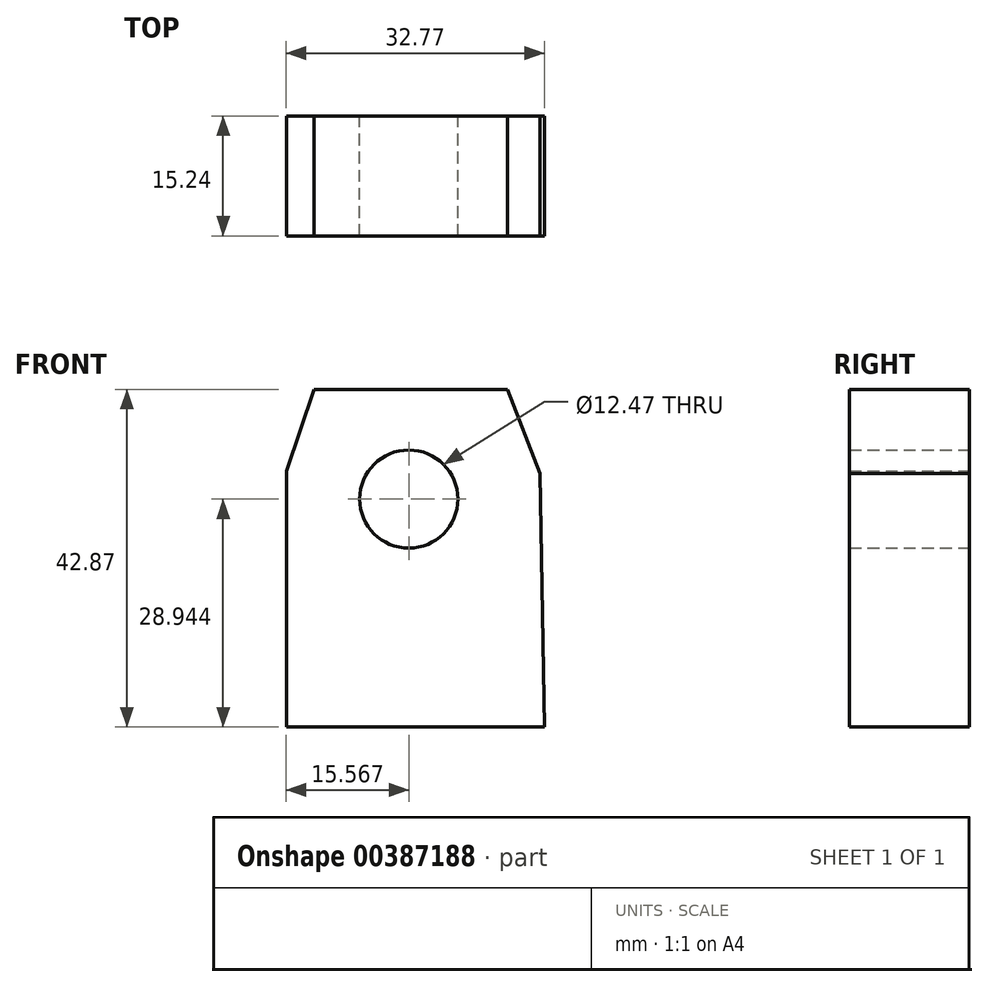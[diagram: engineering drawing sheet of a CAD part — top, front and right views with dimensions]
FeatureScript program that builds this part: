
annotation { "Feature Type Name" : "Feature", "Feature Type Description" : "" }
export const myFeature = defineFeature(function(context is Context, id is Id, definition is map)
    precondition{}
    {
        {
            var Q0;
            Q0=qCreatedBy(makeId("Front.planeOp"),FACE);
            var sketch = newSketch(context, id + "F0", { "sketchPlane" : qUnion([Q0])});
            skLineSegment(sketch, "E0", {"start": v(-19.39, 30.31) * mm, "end": v(5.19, 30.31) * mm});
            skLineSegment(sketch, "E1", {"start": v(5.19, 30.31) * mm, "end": v(9.28, 19.66) * mm});
            skLineSegment(sketch, "E2", {"start": v(-19.39, 30.31) * mm, "end": v(-22.94, 19.93) * mm});
            skPoint(sketch, "E3.end.orphan", {"position": v(11.2, -5.73) * mm});
            skPoint(sketch, "E3.start.orphan", {"position": v(-22.94, -5.73) * mm});
            skLineSegment(sketch, "E4", {"start": v(-22.94, 19.93) * mm, "end": v(-22.94, -12.56) * mm});
            skLineSegment(sketch, "E5", {"start": v(-22.94, -12.56) * mm, "end": v(9.83, -12.56) * mm});
            skLineSegment(sketch, "E6", {"start": v(9.28, 19.66) * mm, "end": v(9.83, -12.56) * mm});
            skCircle(sketch, "E7", {"center": v(-7.37, 16.38) * mm, "radius": 6.23 * mm});
            skSolve(sketch);
        }
        {
            var Q0;
            Q0 = qSketchRegion(id + "F0", true);
            extrude(context, id + "F1", {"entities" : qUnion([Q0]), "depth" : 15.24 * mm});
        }
    });
